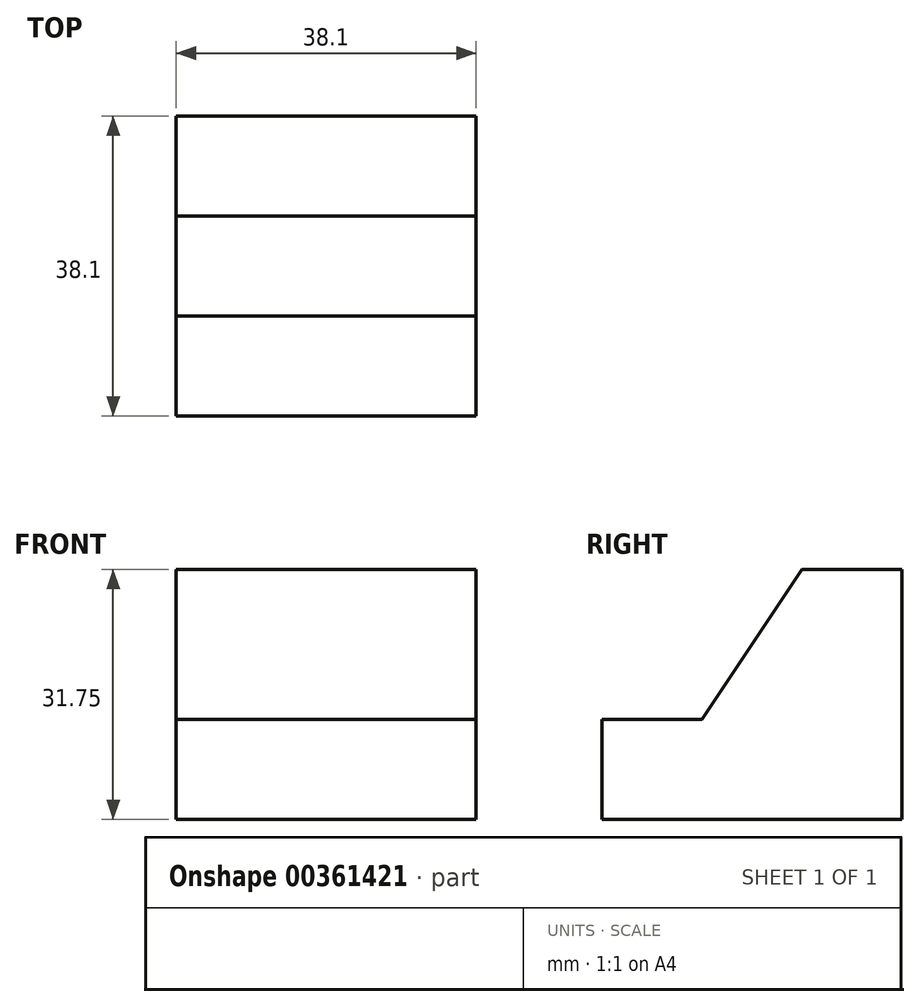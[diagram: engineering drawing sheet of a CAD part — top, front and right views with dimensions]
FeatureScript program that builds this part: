
annotation { "Feature Type Name" : "Feature", "Feature Type Description" : "" }
export const myFeature = defineFeature(function(context is Context, id is Id, definition is map)
    precondition{}
    {
        {
            var Q0;
            Q0=qCreatedBy(makeId("Right.planeOp"),FACE);
            var sketch = newSketch(context, id + "F0", { "sketchPlane" : qUnion([Q0])});
            skLineSegment(sketch, "E0", {"start": v(0, 0) * mm, "end": v(0, 12.7) * mm});
            skLineSegment(sketch, "E1", {"start": v(0, 0) * mm, "end": v(38.1, 0) * mm});
            skLineSegment(sketch, "E2", {"start": v(38.1, 0) * mm, "end": v(38.1, 31.75) * mm});
            skLineSegment(sketch, "E3", {"start": v(38.1, 31.75) * mm, "end": v(25.4, 31.75) * mm});
            skLineSegment(sketch, "E4", {"start": v(0, 12.7) * mm, "end": v(12.7, 12.7) * mm});
            skLineSegment(sketch, "E5", {"start": v(12.7, 12.7) * mm, "end": v(25.4, 31.75) * mm});
            skSolve(sketch);
        }
        {
            var Q0;
            Q0 = qSketchRegion(id + "F0", true);
            extrude(context, id + "F1", {"entities" : qUnion([Q0]), "depth" : 38.1 * mm});
        }
    });
